# Revit family: Bali 4 tubes LOD200
name_source: partatom
category: Equipement de génie climatique
units: mm (PartAtom-declared; Revit-internal decimal feet)

## family parameters
Basée sur le plan de construction = Oui
Classification = Aucun
Cote de connecteur circulaire = Utiliser le diamètre
Couper avec des vides une fois chargée = Non
Numéro OmniClass = 23.75.70.17.27
Partagée = Non
Point de calcul de pièce = Non
Titre OmniClass = Fan Coil Units
Toujours verticalement = Non
Type d'élément = Normal

## types (2) — shared parameters
Elévation par défaut = 1219 mm
Fabricant = AIRCALO
Nominal Voltage = 230 V
Note d'identification = LOG200
rayon bas dalle = 50 mm  [stored 0.164042 ft]
rayon haut dalle = 100 mm  [stored 0.328084 ft]
Ø1 = 19 mm  [stored 0.062336 ft]
Ø1 inter = 18 mm  [stored 0.0590551 ft]
Ø2 = 19 mm  [stored 0.062336 ft]
Ø2 inter = 18 mm  [stored 0.0590551 ft]

## per-type parameters (varying)
- Bali 60 4 tubes LOD200: 3=363 mm; Masse=32; Modèle=BALI 60; Motor Power absorbed=80 W; area bas=588 mm; area droite=438 mm; area gauche=438 mm; area haut=438 mm; batt elec aircalo=383 mm; decalage sortie air=15 mm  [stored 0.0492126 ft]; distance bord bac aux=93 mm  [stored 0.305118 ft]; distance bord condensat=118 mm; distance bord connexion=161 mm  [stored 0.528215 ft]; distance centre debut air neuf=350 mm  [stored 1.14829 ft]; distance centre milieu air neuf=450 mm  [stored 1.47638 ft]; distance haut condensat=112 mm  [stored 0.367454 ft]; entraxe fixation hauteur /2=140 mm  [stored 0.459318 ft]; entraxe fixation/2=340 mm  [stored 1.11549 ft]; epaisseur sortie air=34 mm; hauteur=575 mm; hauteur connexion exterieur=110 mm  [stored 0.360892 ft]; hauteur connexion interieur=110 mm  [stored 0.360892 ft]; hauteur dalle=680 mm; hauteur/2=288 mm; largeur=575 mm; largeur air=380 mm; largeur dalle=680 mm; longueur connexion=320 mm
- Bali 90 4 tubes LOD200: 3=490 mm  [stored 1.60761 ft]; Masse=53; Modèle=BALI 90; Motor Power absorbed=362 W; area bas=715 mm; area droite=565 mm  [stored 1.85367 ft]; area gauche=565 mm  [stored 1.85367 ft]; area haut=565 mm  [stored 1.85367 ft]; batt elec aircalo=510 mm  [stored 1.67323 ft]; decalage sortie air=30 mm  [stored 0.0984252 ft]; distance bord bac aux=92 mm; distance bord condensat=143 mm; distance bord connexion=158 mm; distance centre debut air neuf=530 mm  [stored 1.73885 ft]; distance centre milieu air neuf=630 mm  [stored 2.06693 ft]; distance haut condensat=95 mm; entraxe fixation hauteur /2=243 mm; entraxe fixation/2=432 mm; epaisseur sortie air=60 mm  [stored 0.19685 ft]; hauteur=830 mm; hauteur connexion exterieur=100 mm  [stored 0.328084 ft]; hauteur connexion interieur=108 mm  [stored 0.354331 ft]; hauteur dalle=980 mm; hauteur/2=415 mm  [stored 1.36155 ft]; largeur=830 mm; largeur air=600 mm; largeur dalle=980 mm; longueur connexion=447 mm

note: [stored X ft] marks values corroborated as IEEE doubles in the binary element streams (Revit-internal decimal feet)
